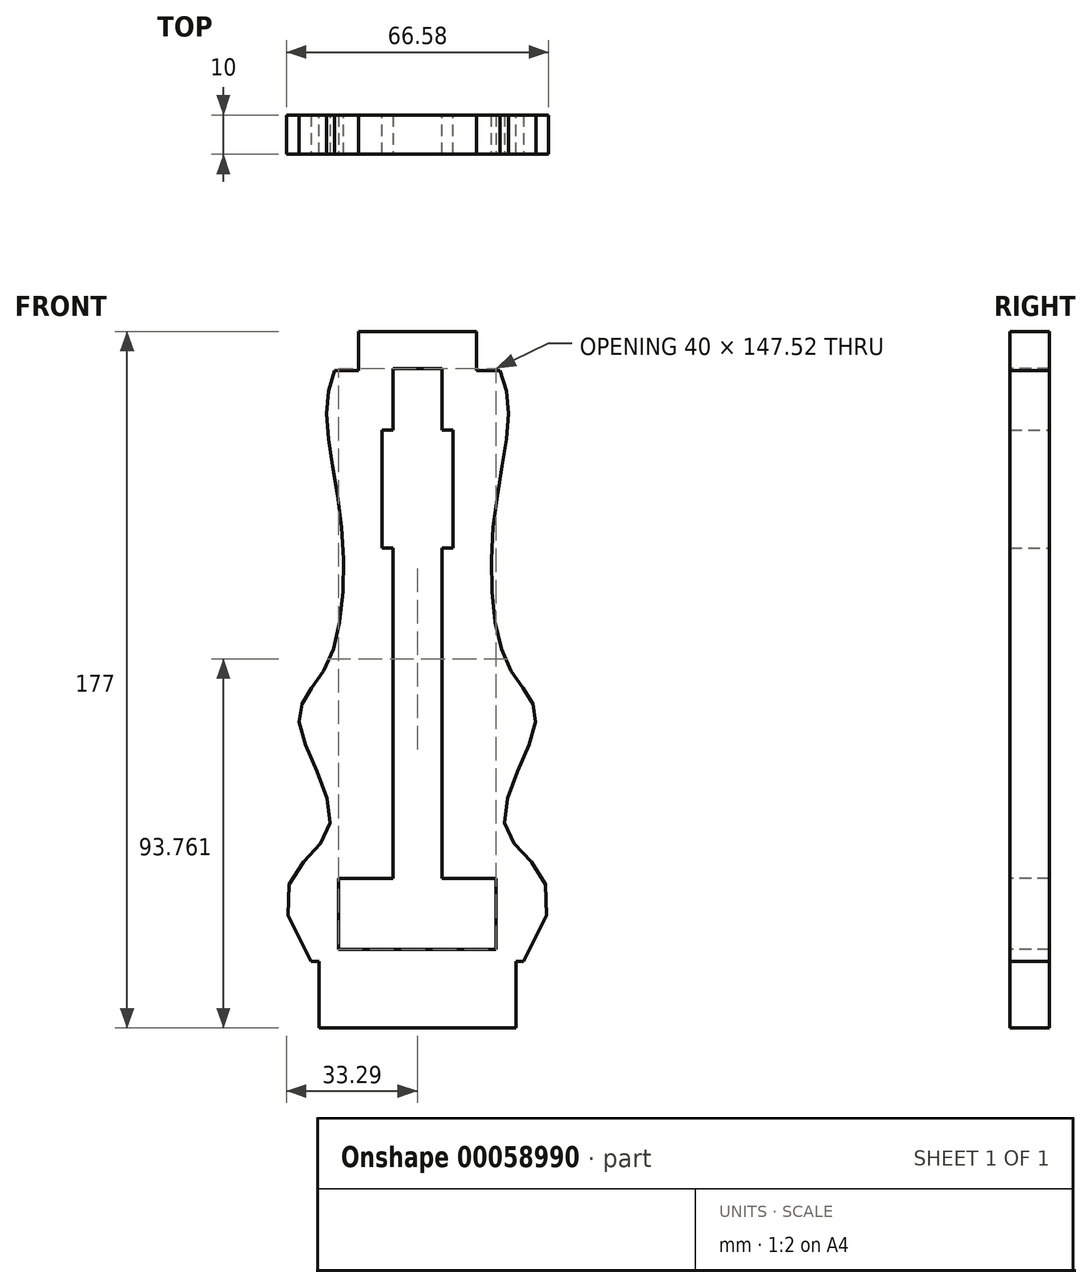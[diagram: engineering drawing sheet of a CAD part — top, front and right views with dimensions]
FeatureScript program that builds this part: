
annotation { "Feature Type Name" : "Feature", "Feature Type Description" : "" }
export const myFeature = defineFeature(function(context is Context, id is Id, definition is map)
    precondition{}
    {
        {
            var Q0;
            Q0=qCreatedBy(makeId("Front.planeOp"),FACE);
            var sketch = newSketch(context, id + "F0", { "sketchPlane" : qUnion([Q0])});
            skLineSegment(sketch, "E0.rect.bottom", {"start": v(-25, 0) * mm, "end": v(-15, 0) * mm});
            skLineSegment(sketch, "E0.rect.top", {"start": v(-25, -17) * mm, "end": v(25, -17) * mm});
            skLineSegment(sketch, "E0.rect.left", {"start": v(-25, 0) * mm, "end": v(-25, -17) * mm});
            skLineSegment(sketch, "E0.rect.right", {"start": v(25, 0) * mm, "end": v(25, -17) * mm});
            skPoint(sketch, "E0.rect.middle", {"position": v(0, -8.5) * mm});
            skLineSegment(sketch, "E1.rect.top", {"start": v(-15, 160) * mm, "end": v(15, 160) * mm});
            skLineSegment(sketch, "E1.rect.left", {"start": v(-15, 0) * mm, "end": v(-15, 160) * mm});
            skLineSegment(sketch, "E1.rect.right", {"start": v(15, 0) * mm, "end": v(15, 160) * mm});
            skPoint(sketch, "E1.rect.middle", {"position": v(0, 80) * mm});
            skLineSegment(sketch, "E2.trimOffspring", {"start": v(15, 0) * mm, "end": v(25, 0) * mm});
            skLineSegment(sketch, "E3.rect.bottom", {"start": v(10, 21) * mm, "end": v(-10, 21) * mm});
            skLineSegment(sketch, "E3.rect.top", {"start": v(10, 3) * mm, "end": v(-10, 3) * mm});
            skLineSegment(sketch, "E3.rect.left", {"start": v(10, 21) * mm, "end": v(10, 3) * mm});
            skLineSegment(sketch, "E3.rect.right", {"start": v(-10, 21) * mm, "end": v(-10, 3) * mm});
            skPoint(sketch, "E3.rect.middle", {"position": v(0, 12) * mm});
            skLineSegment(sketch, "E4.rect.bottom", {"start": v(9, 135) * mm, "end": v(-9, 135) * mm});
            skLineSegment(sketch, "E4.rect.top", {"start": v(9, 105) * mm, "end": v(-9, 105) * mm});
            skLineSegment(sketch, "E4.rect.left", {"start": v(9, 135) * mm, "end": v(9, 105) * mm});
            skLineSegment(sketch, "E4.rect.right", {"start": v(-9, 135) * mm, "end": v(-9, 105) * mm});
            skPoint(sketch, "E4.rect.middle", {"position": v(0, 120) * mm});
            skSolve(sketch);
        }
        {
            var Q0;
            Q0 = qSketchRegion(id + "F0", true);
            extrude(context, id + "F1", {"entities" : qUnion([Q0]), "depth" : 10 * mm});
        }
        {
            var Q0;
            Q0=makeQuery(id+"F1.opExtrude","CAP_FACE",FACE,{"disambiguationData":[OSD([sQuery(id+"F0.wireOp",EDGE,"E0.rect.bottom"),sQuery(id+"F0.wireOp",EDGE,"E0.rect.top"),sQuery(id+"F0.wireOp",EDGE,"E0.rect.left"),sQuery(id+"F0.wireOp",EDGE,"E0.rect.right"),sQuery(id+"F0.wireOp",EDGE,"E1.rect.top"),sQuery(id+"F0.wireOp",EDGE,"E1.rect.left"),sQuery(id+"F0.wireOp",EDGE,"E1.rect.right"),sQuery(id+"F0.wireOp",EDGE,"E2.trimOffspring"),sQuery(id+"F0.wireOp",EDGE,"E3.rect.bottom"),sQuery(id+"F0.wireOp",EDGE,"E3.rect.top"),sQuery(id+"F0.wireOp",EDGE,"E3.rect.left"),sQuery(id+"F0.wireOp",EDGE,"E3.rect.right"),sQuery(id+"F0.wireOp",EDGE,"E4.rect.bottom"),sQuery(id+"F0.wireOp",EDGE,"E4.rect.top"),sQuery(id+"F0.wireOp",EDGE,"E4.rect.left"),sQuery(id+"F0.wireOp",EDGE,"E4.rect.right")])],"isStart":false});
            var sketch = newSketch(context, id + "F2", { "sketchPlane" : qUnion([Q0])});
            skFitSpline(sketch, "E5", {"points": [v(-15, 160) * mm, v(-22.83, 143.6) * mm, v(-19.43, 111.92) * mm, v(-23.14, 74.95) * mm, v(-30.08, 61.02) * mm, v(-22.52, 33.52) * mm, v(-27, 0) * mm], "startDerivative": vector(-76.58, -105.87) * mm, "endDerivative": vector(245.27, -350.23) * mm});
            skLineSegment(sketch, "E6", {"start": v(-15, 150) * mm, "end": v(-15, 0) * mm});
            skLineSegment(sketch, "E7", {"start": v(-15, 0) * mm, "end": v(-27, 0) * mm});
            skLineSegment(sketch, "E8.MirrorCS", {"start": v(15, 150) * mm, "end": v(15, 0) * mm});
            skLineSegment(sketch, "E9.MirrorCS", {"start": v(15, 0) * mm, "end": v(27, 0) * mm});
            skFitSpline(sketch, "E10.MirrorCS", {"points": [v(15, 160) * mm, v(22.83, 143.6) * mm, v(19.43, 111.92) * mm, v(23.14, 74.95) * mm, v(30.08, 61.02) * mm, v(22.52, 33.52) * mm, v(27, 0) * mm], "startDerivative": vector(76.58, -105.87) * mm, "endDerivative": vector(-245.27, -350.23) * mm});
            skLineSegment(sketch, "E11", {"start": v(15, 150) * mm, "end": v(-15, 150) * mm, "construction": true});
            skLineSegment(sketch, "E12", {"start": v(15, 150) * mm, "end": v(21.03, 150) * mm});
            skLineSegment(sketch, "E13", {"start": v(-15, 150) * mm, "end": v(-21.03, 150) * mm});
            skSolve(sketch);
        }
        {
            var Q0;
            Q0 = qSketchRegion(id + "F2", true);
            extrude(context, id + "F3", {"entities" : qUnion([Q0]), "operationType" : NewBodyOperationType.ADD, "oppositeDirection" : true, "depth" : 10 * mm});
        }
        {
            var Q0;
            Q0=makeQuery(id+"F3.boolean.opBoolean","MERGE",FACE,{"derivedFrom":[makeQuery(id+"F1.opExtrude","CAP_FACE",FACE,{"disambiguationData":[OSD([sQuery(id+"F0.wireOp",EDGE,"E0.rect.bottom"),sQuery(id+"F0.wireOp",EDGE,"E0.rect.top"),sQuery(id+"F0.wireOp",EDGE,"E0.rect.left"),sQuery(id+"F0.wireOp",EDGE,"E0.rect.right"),sQuery(id+"F0.wireOp",EDGE,"E1.rect.top"),sQuery(id+"F0.wireOp",EDGE,"E1.rect.left"),sQuery(id+"F0.wireOp",EDGE,"E1.rect.right"),sQuery(id+"F0.wireOp",EDGE,"E2.trimOffspring"),sQuery(id+"F0.wireOp",EDGE,"E3.rect.bottom"),sQuery(id+"F0.wireOp",EDGE,"E3.rect.top"),sQuery(id+"F0.wireOp",EDGE,"E3.rect.left"),sQuery(id+"F0.wireOp",EDGE,"E3.rect.right"),sQuery(id+"F0.wireOp",EDGE,"E4.rect.bottom"),sQuery(id+"F0.wireOp",EDGE,"E4.rect.top"),sQuery(id+"F0.wireOp",EDGE,"E4.rect.left"),sQuery(id+"F0.wireOp",EDGE,"E4.rect.right")])],"isStart":false}),makeQuery(id+"F3.opExtrude","CAP_FACE",FACE,{"disambiguationData":[OSD([sQuery(id+"F2.wireOp",EDGE,"E5"),sQuery(id+"F2.wireOp",EDGE,"E6"),sQuery(id+"F2.wireOp",EDGE,"E7"),sQuery(id+"F2.wireOp",EDGE,"E13")])],"isStart":true}),makeQuery(id+"F3.opExtrude","CAP_FACE",FACE,{"disambiguationData":[OSD([sQuery(id+"F2.wireOp",EDGE,"E8.MirrorCS"),sQuery(id+"F2.wireOp",EDGE,"E9.MirrorCS"),sQuery(id+"F2.wireOp",EDGE,"E10.MirrorCS"),sQuery(id+"F2.wireOp",EDGE,"E12")])],"isStart":true})]});
            var sketch = newSketch(context, id + "F4", { "sketchPlane" : qUnion([Q0])});
            skLineSegment(sketch, "E14.top", {"start": v(-6.24, 21) * mm, "end": v(6.24, 21) * mm});
            skLineSegment(sketch, "E14.left", {"start": v(-6.24, 150.52) * mm, "end": v(-6.24, 21) * mm});
            skLineSegment(sketch, "E14.right", {"start": v(6.24, 150.52) * mm, "end": v(6.24, 21) * mm});
            skLineSegment(sketch, "E15", {"start": v(-6.24, 150.52) * mm, "end": v(6.24, 150.52) * mm});
            skSolve(sketch);
        }
        {
            var Q0;
            Q0 = qSketchRegion(id + "F4", true);
            extrude(context, id + "F5", {"entities" : qUnion([Q0]), "operationType" : NewBodyOperationType.REMOVE, "oppositeDirection" : true, "depth" : 25 * mm});
        }
        {
            var Q0;
            Q0=makeQuery(id+"F3.boolean.opBoolean","MERGE",FACE,{"derivedFrom":[makeQuery(id+"F1.opExtrude","CAP_FACE",FACE,{"disambiguationData":[OSD([sQuery(id+"F0.wireOp",EDGE,"E0.rect.bottom"),sQuery(id+"F0.wireOp",EDGE,"E0.rect.top"),sQuery(id+"F0.wireOp",EDGE,"E0.rect.left"),sQuery(id+"F0.wireOp",EDGE,"E0.rect.right"),sQuery(id+"F0.wireOp",EDGE,"E1.rect.top"),sQuery(id+"F0.wireOp",EDGE,"E1.rect.left"),sQuery(id+"F0.wireOp",EDGE,"E1.rect.right"),sQuery(id+"F0.wireOp",EDGE,"E2.trimOffspring"),sQuery(id+"F0.wireOp",EDGE,"E3.rect.bottom"),sQuery(id+"F0.wireOp",EDGE,"E3.rect.top"),sQuery(id+"F0.wireOp",EDGE,"E3.rect.left"),sQuery(id+"F0.wireOp",EDGE,"E3.rect.right"),sQuery(id+"F0.wireOp",EDGE,"E4.rect.bottom"),sQuery(id+"F0.wireOp",EDGE,"E4.rect.top"),sQuery(id+"F0.wireOp",EDGE,"E4.rect.left"),sQuery(id+"F0.wireOp",EDGE,"E4.rect.right")])],"isStart":false}),makeQuery(id+"F3.opExtrude","CAP_FACE",FACE,{"disambiguationData":[OSD([sQuery(id+"F2.wireOp",EDGE,"E5"),sQuery(id+"F2.wireOp",EDGE,"E6"),sQuery(id+"F2.wireOp",EDGE,"E7"),sQuery(id+"F2.wireOp",EDGE,"E13")])],"isStart":true}),makeQuery(id+"F3.opExtrude","CAP_FACE",FACE,{"disambiguationData":[OSD([sQuery(id+"F2.wireOp",EDGE,"E8.MirrorCS"),sQuery(id+"F2.wireOp",EDGE,"E9.MirrorCS"),sQuery(id+"F2.wireOp",EDGE,"E10.MirrorCS"),sQuery(id+"F2.wireOp",EDGE,"E12")])],"isStart":true})]});
            var sketch = newSketch(context, id + "F6", { "sketchPlane" : qUnion([Q0])});
            skLineSegment(sketch, "E16.bottom", {"start": v(-20, 21) * mm, "end": v(-10, 21) * mm});
            skLineSegment(sketch, "E16.top", {"start": v(-20, 3) * mm, "end": v(-10, 3) * mm});
            skLineSegment(sketch, "E16.left", {"start": v(-20, 21) * mm, "end": v(-20, 3) * mm});
            skLineSegment(sketch, "E16.right", {"start": v(-10, 21) * mm, "end": v(-10, 3) * mm});
            skLineSegment(sketch, "E17.MirrorCS", {"start": v(20, 21) * mm, "end": v(10, 21) * mm});
            skLineSegment(sketch, "E18.MirrorCS", {"start": v(10, 21) * mm, "end": v(10, 3) * mm});
            skLineSegment(sketch, "E19.MirrorCS", {"start": v(20, 21) * mm, "end": v(20, 3) * mm});
            skLineSegment(sketch, "E20.MirrorCS", {"start": v(20, 3) * mm, "end": v(10, 3) * mm});
            skSolve(sketch);
        }
        {
            var Q0;
            Q0 = qSketchRegion(id + "F6", true);
            extrude(context, id + "F7", {"entities" : qUnion([Q0]), "operationType" : NewBodyOperationType.REMOVE, "oppositeDirection" : true, "depth" : 25 * mm});
        }
    });
